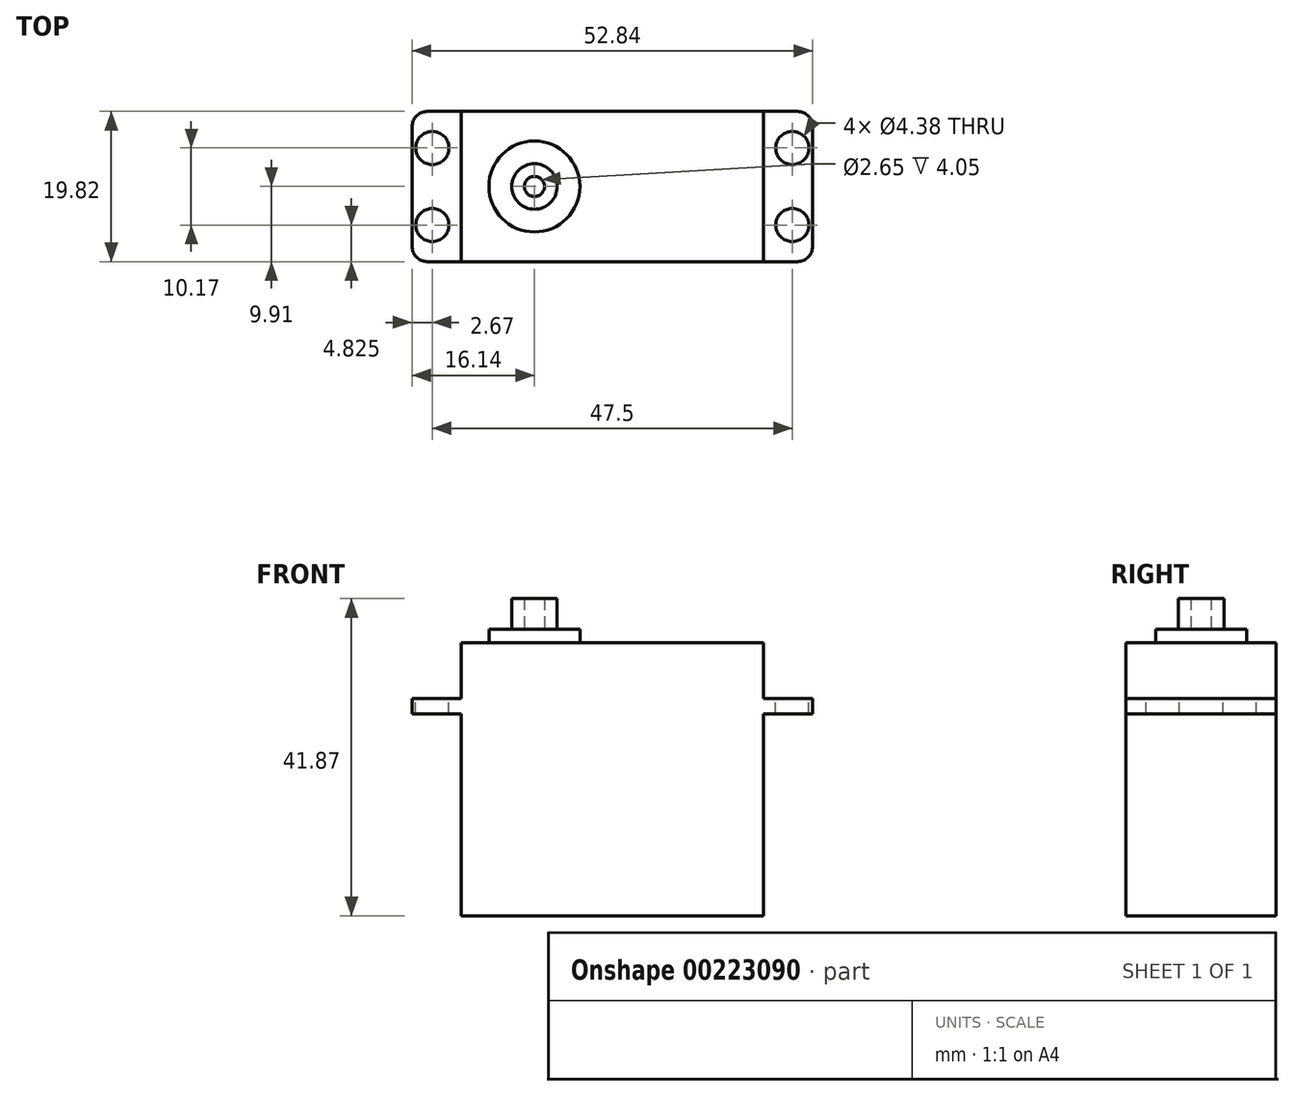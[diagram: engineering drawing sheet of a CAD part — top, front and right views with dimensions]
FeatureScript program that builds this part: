
annotation { "Feature Type Name" : "Feature", "Feature Type Description" : "" }
export const myFeature = defineFeature(function(context is Context, id is Id, definition is map)
    precondition{}
    {
        {
            var Q0;
            Q0=qCreatedBy(makeId("Top.planeOp"),FACE);
            var sketch = newSketch(context, id + "F0", { "sketchPlane" : qUnion([Q0])});
            skLineSegment(sketch, "E0.bottom", {"start": v(0, 0) * mm, "end": v(39.88, 0) * mm});
            skLineSegment(sketch, "E0.top", {"start": v(0, 19.82) * mm, "end": v(39.88, 19.82) * mm});
            skLineSegment(sketch, "E0.left", {"start": v(0, 0) * mm, "end": v(0, 19.82) * mm});
            skLineSegment(sketch, "E0.right", {"start": v(39.88, 0) * mm, "end": v(39.88, 19.82) * mm});
            skSolve(sketch);
        }
        {
            var Q0;
            Q0=makeQuery(id+"F0.imprint","IMPRINT",FACE,{"disambiguationData":[TD([[makeQuery(id+"F0.imprint","IMPRINT",EDGE,{"derivedFrom":sQuery(id+"F0.wireOp",EDGE,"E0.bottom")}),1.0]])]});
            extrude(context, id + "F1", {"entities" : qUnion([Q0]), "depth" : 26.67 * mm});
        }
        {
            var Q0;
            Q0=makeQuery(id+"F1.opExtrude","CAP_FACE",FACE,{"disambiguationData":[OSD([sQuery(id+"F0.wireOp",EDGE,"E0.bottom"),sQuery(id+"F0.wireOp",EDGE,"E0.top"),sQuery(id+"F0.wireOp",EDGE,"E0.left"),sQuery(id+"F0.wireOp",EDGE,"E0.right")])],"isStart":false});
            var sketch = newSketch(context, id + "F2", { "sketchPlane" : qUnion([Q0])});
            skLineSegment(sketch, "E1.bottom", {"start": v(-6.48, 19.82) * mm, "end": v(46.36, 19.82) * mm});
            skLineSegment(sketch, "E1.top", {"start": v(-6.48, 0) * mm, "end": v(46.36, 0) * mm});
            skLineSegment(sketch, "E1.left", {"start": v(-6.48, 19.82) * mm, "end": v(-6.48, 0) * mm});
            skLineSegment(sketch, "E1.right", {"start": v(46.36, 19.82) * mm, "end": v(46.36, 0) * mm});
            skSolve(sketch);
        }
        {
            var Q0;
            {var subQ2=sQuery(id+"F2.wireOp",EDGE,"E1.left");Q0=makeQuery(id+"F2.imprint","IMPRINT",FACE,{"disambiguationData":[TD([[makeQuery(id+"F2.imprint","IMPRINT",EDGE,{"derivedFrom":subQ2}),1.0]])]});}
            var Q1;
            {var subQ1=makeQuery(id+"F1.opExtrude","CAP_EDGE",EDGE,{"disambiguationData":[OSD([sQuery(id+"F0.wireOp",EDGE,"E0.left")])],"isStart":false});Q1=makeQuery(id+"F2.imprint","IMPRINT",FACE,{"disambiguationData":[TD([[makeQuery(id+"F2.imprint","IMPRINT",EDGE,{"derivedFrom":subQ1}),-1.0]])]});}
            var Q2;
            {var subQ2=sQuery(id+"F2.wireOp",EDGE,"E1.right");Q2=makeQuery(id+"F2.imprint","IMPRINT",FACE,{"disambiguationData":[TD([[makeQuery(id+"F2.imprint","IMPRINT",EDGE,{"derivedFrom":subQ2}),-1.0]])]});}
            extrude(context, id + "F3", {"entities" : qUnion([Q0, Q1, Q2]), "operationType" : NewBodyOperationType.ADD, "depth" : 2 * mm});
        }
        {
            var Q0;
            Q0=makeQuery(id+"F3.opExtrude","CAP_FACE",FACE,{"disambiguationData":[OSD([sQuery(id+"F2.wireOp",EDGE,"E1.bottom"),sQuery(id+"F2.wireOp",EDGE,"E1.top"),sQuery(id+"F2.wireOp",EDGE,"E1.left"),sQuery(id+"F2.wireOp",EDGE,"E1.right")])],"isStart":false});
            var sketch = newSketch(context, id + "F4", { "sketchPlane" : qUnion([Q0])});
            skPoint(sketch, "E2.0", {"position": v(0, 0) * mm});
            skPoint(sketch, "E3.0", {"position": v(39.88, 19.82) * mm});
            skLineSegment(sketch, "E4.bottom", {"start": v(0, 0) * mm, "end": v(39.88, 0) * mm});
            skLineSegment(sketch, "E4.top", {"start": v(0, 19.82) * mm, "end": v(39.88, 19.82) * mm});
            skLineSegment(sketch, "E4.left", {"start": v(0, 0) * mm, "end": v(0, 19.82) * mm});
            skLineSegment(sketch, "E4.right", {"start": v(39.88, 0) * mm, "end": v(39.88, 19.82) * mm});
            skSolve(sketch);
        }
        {
            var Q0;
            Q0 = qSketchRegion(id + "F4", true);
            extrude(context, id + "F5", {"entities" : qUnion([Q0]), "operationType" : NewBodyOperationType.ADD, "depth" : 7.35 * mm});
        }
        {
            var Q0;
            Q0=makeQuery(id+"F5.opExtrude","CAP_FACE",FACE,{"disambiguationData":[OSD([sQuery(id+"F4.wireOp",EDGE,"E4.bottom"),sQuery(id+"F4.wireOp",EDGE,"E4.top"),sQuery(id+"F4.wireOp",EDGE,"E4.left"),sQuery(id+"F4.wireOp",EDGE,"E4.right")])],"isStart":false});
            var sketch = newSketch(context, id + "F6", { "sketchPlane" : qUnion([Q0])});
            skLineSegment(sketch, "E5", {"start": v(0, 9.91) * mm, "end": v(39.88, 9.91) * mm, "construction": true});
            skCircle(sketch, "E6", {"center": v(9.66, 9.9) * mm, "radius": 6 * mm});
            skSolve(sketch);
        }
        {
            var Q0;
            Q0=makeQuery(id+"F6.imprint","IMPRINT",FACE,{"disambiguationData":[TD([[makeQuery(id+"F6.imprint","IMPRINT",EDGE,{"derivedFrom":sQuery(id+"F6.wireOp",EDGE,"E6")}),1.0]])]});
            var Q1;
            Q1=sQuery(id+"F6.wireOp",EDGE,"E6");
            extrude(context, id + "F7", {"entities" : qUnion([Q0]), "operationType" : NewBodyOperationType.ADD, "surfaceEntities" : qUnion([Q1]), "depth" : 1.8 * mm});
        }
        {
            var Q0;
            Q0=makeQuery(id+"F7.opExtrude","CAP_FACE",FACE,{"disambiguationData":[OSD([sQuery(id+"F6.wireOp",EDGE,"E6")])],"isStart":false});
            var sketch = newSketch(context, id + "F8", { "sketchPlane" : qUnion([Q0])});
            skCircle(sketch, "E7.0", {"center": v(9.66, 9.9) * mm, "radius": 6 * mm, "construction": true});
            skCircle(sketch, "E8", {"center": v(9.66, 9.9) * mm, "radius": 3 * mm});
            skCircle(sketch, "E9", {"center": v(9.66, 9.9) * mm, "radius": 1.33 * mm});
            skSolve(sketch);
        }
        {
            var Q0;
            Q0=makeQuery(id+"F8.imprint","IMPRINT",FACE,{"disambiguationData":[TD([[makeQuery(id+"F8.imprint","IMPRINT",EDGE,{"derivedFrom":sQuery(id+"F8.wireOp",EDGE,"E8")}),1.0]])]});
            var Q1;
            Q1=sQuery(id+"F8.wireOp",EDGE,"E8");
            extrude(context, id + "F9", {"entities" : qUnion([Q0]), "operationType" : NewBodyOperationType.ADD, "surfaceEntities" : qUnion([Q1]), "depth" : 4.05 * mm});
        }
        {
            var Q0;
            {var subQ0=sQuery(id+"F2.wireOp",EDGE,"E1.top");var subQ1=sQuery(id+"F2.wireOp",EDGE,"E1.bottom");var subQ2=sQuery(id+"F2.wireOp",EDGE,"E1.left");Q0=makeQuery(id+"F5.boolean.opBoolean","SPLIT",FACE,{"disambiguationData":[TD([makeQuery(id+"F3.opExtrude","SWEPT_FACE",FACE,{"disambiguationData":[OSD([subQ2])]})])],"derivedFrom":makeQuery(id+"F3.opExtrude","CAP_FACE",FACE,{"disambiguationData":[OSD([subQ1,subQ0,subQ2,sQuery(id+"F2.wireOp",EDGE,"E1.right")])],"isStart":false})});}
            var sketch = newSketch(context, id + "F10", { "sketchPlane" : qUnion([Q0])});
            skCircle(sketch, "E10", {"center": v(-3.8, 4.83) * mm, "radius": 2.19 * mm});
            skLineSegment(sketch, "E11", {"start": v(-6.48, 9.91) * mm, "end": v(0, 9.91) * mm, "construction": true});
            skCircle(sketch, "E12.MirrorC", {"center": v(-3.81, 15) * mm, "radius": 2.19 * mm});
            skPoint(sketch, "E13.0", {"position": v(39.88, 0) * mm});
            skLineSegment(sketch, "E14", {"start": v(0, 0) * mm, "end": v(39.88, 0) * mm, "construction": true});
            skLineSegment(sketch, "E15", {"start": v(19.94, 0) * mm, "end": v(19.94, 25.28) * mm, "construction": true});
            skCircle(sketch, "E16.MirrorC", {"center": v(43.69, 4.83) * mm, "radius": 2.19 * mm});
            skCircle(sketch, "E17.MirrorC", {"center": v(43.69, 15) * mm, "radius": 2.19 * mm});
            skCircle(sketch, "E18.0", {"center": v(9.66, 9.9) * mm, "radius": 1.33 * mm, "construction": true});
            skSolve(sketch);
        }
        {
            var Q0;
            Q0 = qSketchRegion(id + "F10", true);
            extrude(context, id + "F11", {"entities" : qUnion([Q0]), "operationType" : NewBodyOperationType.REMOVE, "oppositeDirection" : true, "depth" : 25 * mm});
        }
        {
            var Q0;
            Q0=makeQuery(id+"F3.opExtrude","SWEPT_EDGE",EDGE,{"disambiguationData":[OSD([sQuery(id+"F2.wireOp",EDGE,"E1.bottom"),sQuery(id+"F2.wireOp",EDGE,"E1.left")])]});
            var Q1;
            Q1=makeQuery(id+"F3.opExtrude","SWEPT_EDGE",EDGE,{"disambiguationData":[OSD([sQuery(id+"F2.wireOp",EDGE,"E1.bottom"),sQuery(id+"F2.wireOp",EDGE,"E1.right")])]});
            var Q2;
            Q2=makeQuery(id+"F3.opExtrude","SWEPT_EDGE",EDGE,{"disambiguationData":[OSD([sQuery(id+"F2.wireOp",EDGE,"E1.top"),sQuery(id+"F2.wireOp",EDGE,"E1.right")])]});
            var Q3;
            Q3=makeQuery(id+"F3.opExtrude","SWEPT_EDGE",EDGE,{"disambiguationData":[OSD([sQuery(id+"F2.wireOp",EDGE,"E1.top"),sQuery(id+"F2.wireOp",EDGE,"E1.left")])]});
            fillet(context, id + "F12", {"entities" : qUnion([Q0, Q1, Q2, Q3]), "radius" : 2 * mm, "tangentPropagation" : true, "allowEdgeOverflow" : false});
        }
    });
